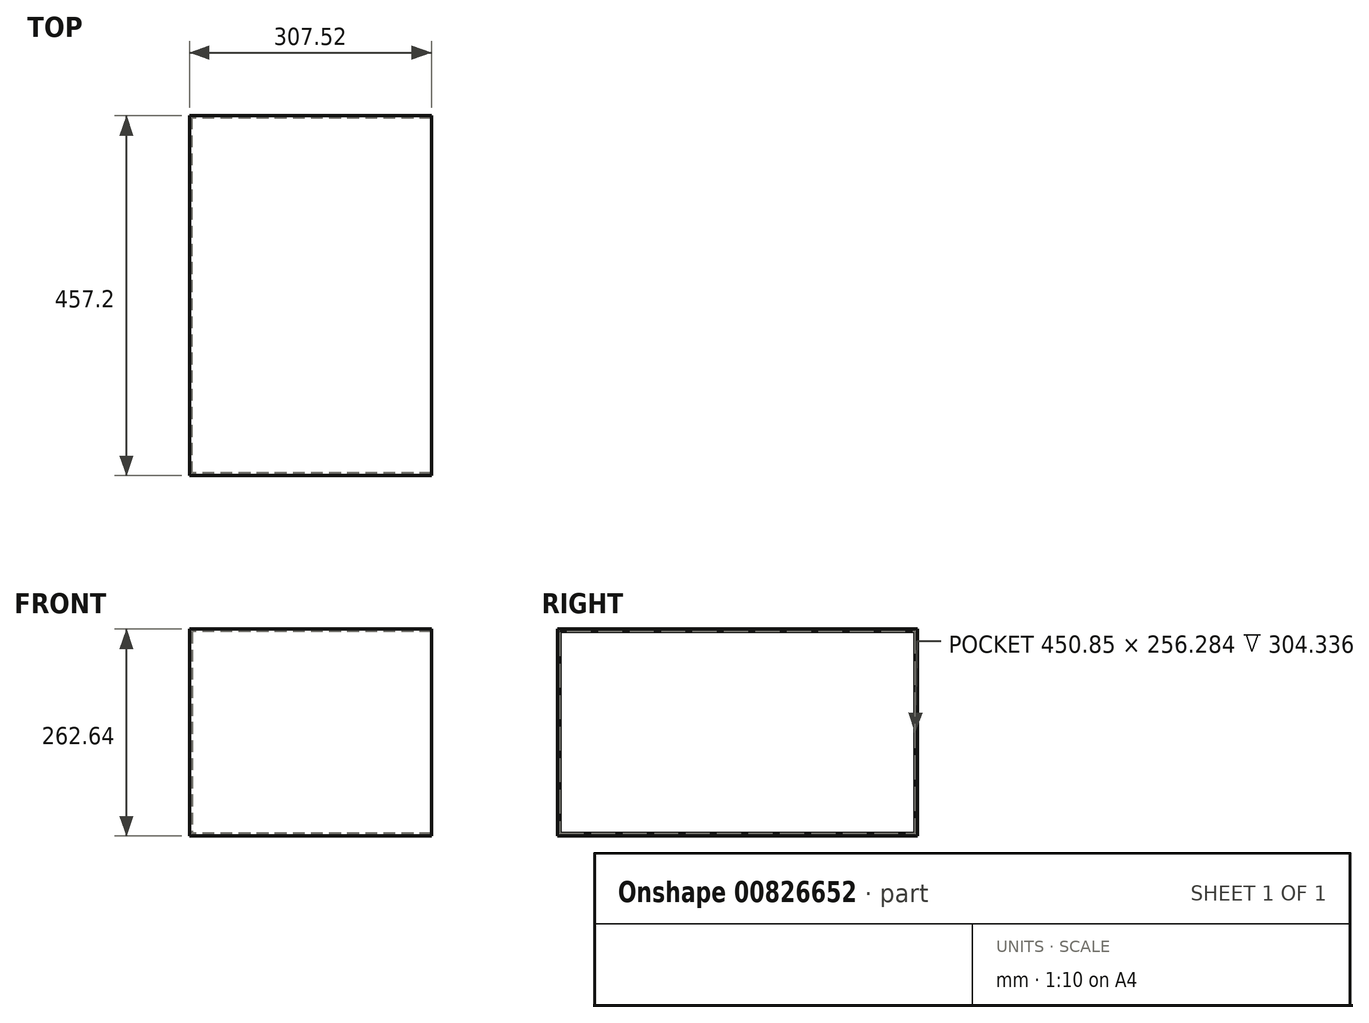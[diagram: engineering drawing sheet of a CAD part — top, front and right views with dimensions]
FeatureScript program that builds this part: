
annotation { "Feature Type Name" : "Feature", "Feature Type Description" : "" }
export const myFeature = defineFeature(function(context is Context, id is Id, definition is map)
    precondition{}
    {
        {
            var Q0;
            Q0=qCreatedBy(makeId("Front.planeOp"),FACE);
            var sketch = newSketch(context, id + "F0", { "sketchPlane" : qUnion([Q0])});
            skLineSegment(sketch, "E0.bottom", {"start": v(153.76, 131.32) * mm, "end": v(-153.76, 131.32) * mm});
            skLineSegment(sketch, "E0.top", {"start": v(153.76, -131.32) * mm, "end": v(-153.76, -131.32) * mm});
            skLineSegment(sketch, "E0.left", {"start": v(153.76, 131.32) * mm, "end": v(153.76, -131.32) * mm});
            skLineSegment(sketch, "E0.right", {"start": v(-153.76, 131.32) * mm, "end": v(-153.76, -131.32) * mm});
            skPoint(sketch, "E0.middle", {"position": v(0, 0) * mm});
            skSolve(sketch);
        }
        {
            var Q0;
            Q0=makeQuery(id+"F0.imprint","IMPRINT",FACE,{"disambiguationData":[TD([[makeQuery(id+"F0.imprint","IMPRINT",EDGE,{"derivedFrom":sQuery(id+"F0.wireOp",EDGE,"E0.bottom")}),1.0]])]});
            extrude(context, id + "F1", {"entities" : qUnion([Q0]), "depth" : 457.2 * mm, "offsetDistance" : 25.4 * mm});
        }
        {
            var Q0;
            Q0=makeQuery(id+"F1.opExtrude","SWEPT_FACE",FACE,{"disambiguationData":[OSD([sQuery(id+"F0.wireOp",EDGE,"E0.left")])]});
            shell(context, id + "F2", {"entities" : qUnion([Q0]), "thickness" : 3.17 * mm});
        }
    });
